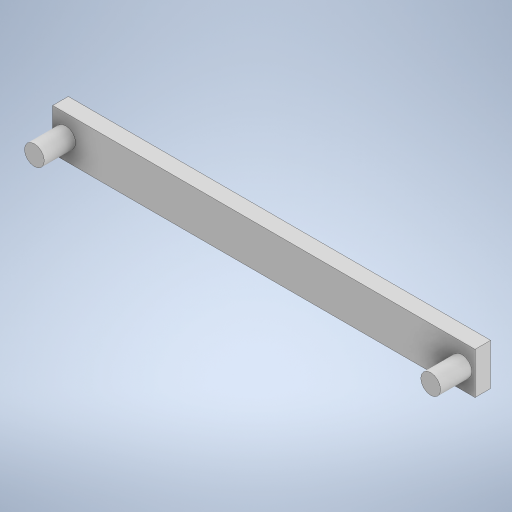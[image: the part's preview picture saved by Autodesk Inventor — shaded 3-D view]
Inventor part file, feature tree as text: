
AUTODESK INVENTOR PART (.ipt)
format: ipt  version: 2024 (Build 280153000, 153)  size: 248,832 bytes
history: native  units: in
note: dims shown in document units (in); Inventor stores cm internally (conversion verified against a paired STEP export)
features: extrude x3, sketch x3
ambient origin geometry x8: Origin, YZ Plane, XZ Plane, XY Plane, X Axis, Y Axis, Z Axis, Center Point
bodies: Solid1 (feature_tree)
feature tree (6):
  extrude  "Extrusion1"  Depth=0.315in
  extrude  "Extrusion2"  Depth=0.1181in
  extrude  "Extrusion3"  Depth=0.2362in TaperAngle=0.0deg
  sketch  "Sketch1"  dims[d0=2.9921in d1=0.315in]
  sketch  "Sketch2"  dims[d2=0.1181in d3=0.0in d4=0.1496in]
  sketch  "Sketch3"  dims[d5=0.1496in d6=0.2362in d7=0.0in d8=0.0984in d9=0.0984in d10=0.1181in d11=0.0in]
